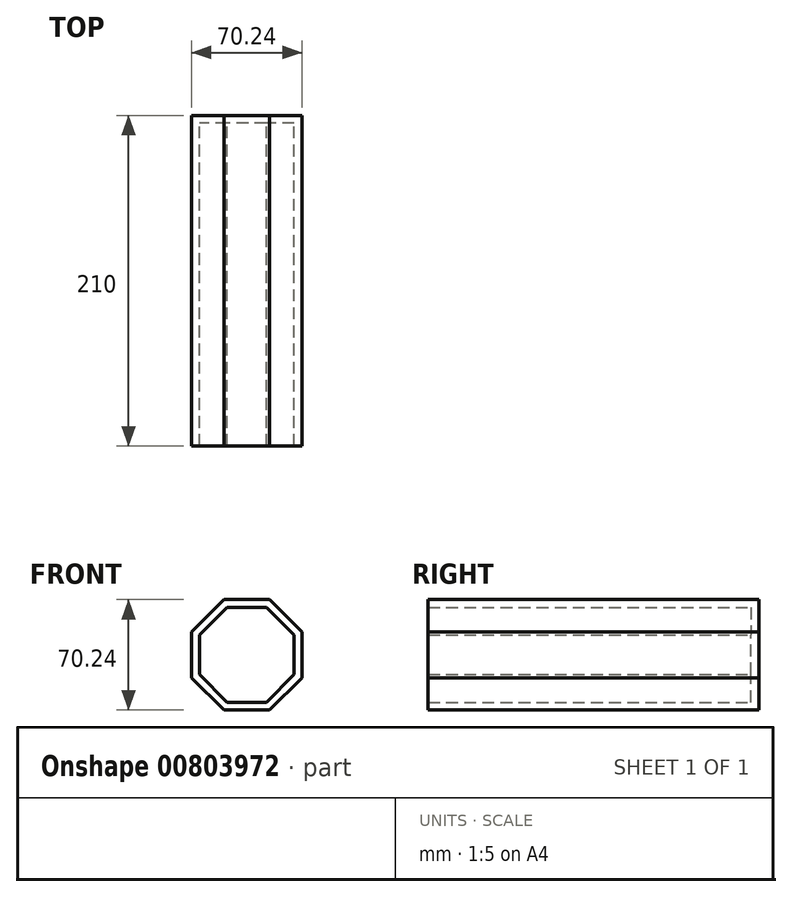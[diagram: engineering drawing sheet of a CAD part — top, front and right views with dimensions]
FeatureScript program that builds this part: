
annotation { "Feature Type Name" : "Feature", "Feature Type Description" : "" }
export const myFeature = defineFeature(function(context is Context, id is Id, definition is map)
    precondition{}
    {
        {
            var Q0;
            Q0=qCreatedBy(makeId("Front.planeOp"),FACE);
            var sketch = newSketch(context, id + "F0", { "sketchPlane" : qUnion([Q0])});
            skCircle(sketch, "E0.cCircle", {"center": v(0, 0) * mm, "radius": 35.12 * mm, "construction": true});
            skLineSegment(sketch, "E0.0", {"start": v(-35.12, -14.55) * mm, "end": v(-35.12, 14.55) * mm});
            skLineSegment(sketch, "E0.1", {"start": v(-35.12, 14.55) * mm, "end": v(-14.55, 35.12) * mm});
            skLineSegment(sketch, "E0.2", {"start": v(-14.55, 35.12) * mm, "end": v(14.55, 35.12) * mm});
            skLineSegment(sketch, "E0.3", {"start": v(14.55, 35.12) * mm, "end": v(35.12, 14.55) * mm});
            skLineSegment(sketch, "E0.4", {"start": v(35.12, 14.55) * mm, "end": v(35.12, -14.55) * mm});
            skLineSegment(sketch, "E0.5", {"start": v(35.12, -14.55) * mm, "end": v(14.55, -35.12) * mm});
            skLineSegment(sketch, "E0.6", {"start": v(14.55, -35.12) * mm, "end": v(-14.55, -35.12) * mm});
            skLineSegment(sketch, "E0.7", {"start": v(-14.55, -35.12) * mm, "end": v(-35.12, -14.55) * mm});
            skPoint(sketch, "E0.0.midPoint", {"position": v(-35.12, 0) * mm});
            skSolve(sketch);
        }
        {
            var Q0;
            Q0=makeQuery(id+"F0.imprint","IMPRINT",FACE,{"disambiguationData":[TD([[makeQuery(id+"F0.imprint","IMPRINT",EDGE,{"derivedFrom":sQuery(id+"F0.wireOp",EDGE,"E0.0")}),-1.0]])]});
            extrude(context, id + "F1", {"entities" : qUnion([Q0]), "depth" : 210 * mm, "offsetDistance" : 25 * mm});
        }
        {
            var Q0;
            Q0=makeQuery(id+"F1.opExtrude","CAP_FACE",FACE,{"disambiguationData":[OSD([sQuery(id+"F0.wireOp",EDGE,"E0.0"),sQuery(id+"F0.wireOp",EDGE,"E0.1"),sQuery(id+"F0.wireOp",EDGE,"E0.2"),sQuery(id+"F0.wireOp",EDGE,"E0.3"),sQuery(id+"F0.wireOp",EDGE,"E0.4"),sQuery(id+"F0.wireOp",EDGE,"E0.5"),sQuery(id+"F0.wireOp",EDGE,"E0.6"),sQuery(id+"F0.wireOp",EDGE,"E0.7")])],"isStart":false});
            shell(context, id + "F2", {"entities" : qUnion([Q0]), "thickness" : 5 * mm});
        }
    });
